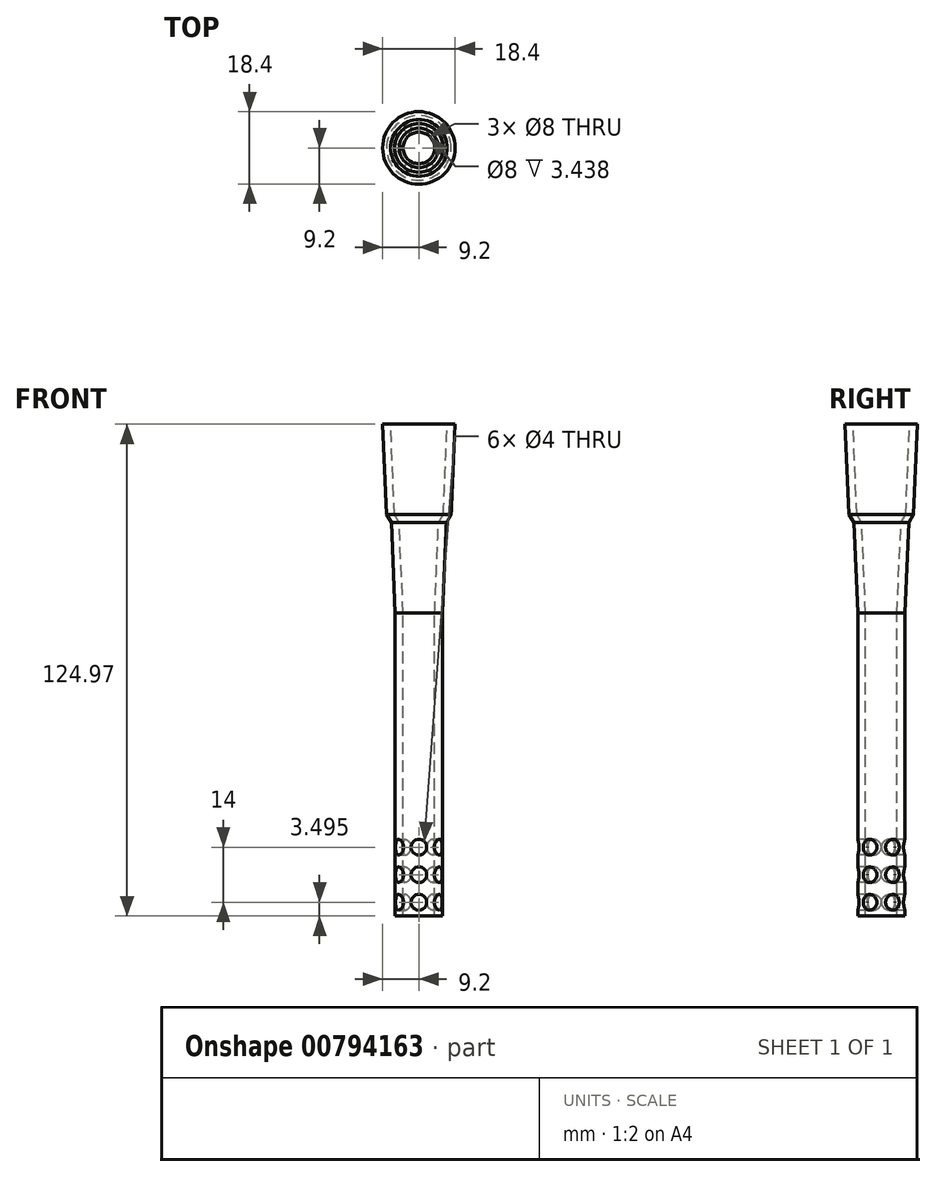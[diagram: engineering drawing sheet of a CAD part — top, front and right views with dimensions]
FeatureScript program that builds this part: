
annotation { "Feature Type Name" : "Feature", "Feature Type Description" : "" }
export const myFeature = defineFeature(function(context is Context, id is Id, definition is map)
    precondition{}
    {
        {
            var Q0;
            Q0=qCreatedBy(makeId("Front.planeOp"),FACE);
            var sketch = newSketch(context, id + "F0", { "sketchPlane" : qUnion([Q0])});
            skLineSegment(sketch, "E0.bottom", {"start": v(0, 29.63) * mm, "end": v(-6, 29.63) * mm});
            skLineSegment(sketch, "E0.top", {"start": v(0, -47.37) * mm, "end": v(-6, -47.37) * mm});
            skLineSegment(sketch, "E0.left", {"start": v(0, 29.63) * mm, "end": v(0, -47.37) * mm});
            skLineSegment(sketch, "E0.right", {"start": v(-6, 29.63) * mm, "end": v(-6, -47.37) * mm});
            skLineSegment(sketch, "E1", {"start": v(-6, 29.63) * mm, "end": v(-7, 52.6) * mm});
            skLineSegment(sketch, "E2", {"start": v(-7, 52.6) * mm, "end": v(0, 52.6) * mm});
            skLineSegment(sketch, "E3", {"start": v(0, 52.6) * mm, "end": v(0, 29.63) * mm});
            skLineSegment(sketch, "E4", {"start": v(0, 77.6) * mm, "end": v(0, 52.6) * mm});
            skLineSegment(sketch, "E5", {"start": v(-5, 52.6) * mm, "end": v(-4, 29.63) * mm});
            skLineSegment(sketch, "E6", {"start": v(-4, 29.63) * mm, "end": v(-4, -47.37) * mm});
            skLineSegment(sketch, "E7", {"start": v(0, 77.6) * mm, "end": v(-7.2, 77.6) * mm});
            skLineSegment(sketch, "E8", {"start": v(-7.2, 77.6) * mm, "end": v(-6.2, 54.63) * mm});
            skLineSegment(sketch, "E9", {"start": v(-6.2, 54.63) * mm, "end": v(0, 54.63) * mm});
            skPoint(sketch, "E9.endSnap0", {"position": v(0, 65.1) * mm});
            skLineSegment(sketch, "E10", {"start": v(-7.2, 77.6) * mm, "end": v(-9.2, 77.6) * mm});
            skLineSegment(sketch, "E11", {"start": v(-9.2, 77.6) * mm, "end": v(-8.2, 54.63) * mm});
            skLineSegment(sketch, "E12", {"start": v(-8.2, 54.63) * mm, "end": v(-6.2, 54.63) * mm});
            skLineSegment(sketch, "E13", {"start": v(-6.2, 54.63) * mm, "end": v(-5, 52.6) * mm});
            skLineSegment(sketch, "E14", {"start": v(-8.2, 54.63) * mm, "end": v(-7, 52.6) * mm});
            skCircle(sketch, "E15", {"center": v(0, -43.87) * mm, "radius": 2 * mm});
            skCircle(sketch, "E16", {"center": v(0, -36.87) * mm, "radius": 2 * mm});
            skCircle(sketch, "E17", {"center": v(0, -29.87) * mm, "radius": 2 * mm});
            skSolve(sketch);
        }
        {
            var Q0;
            Q0=makeQuery(id+"F0.imprint","IMPRINT",FACE,{"disambiguationData":[TD([[makeQuery(id+"F0.imprint","IMPRINT",EDGE,{"derivedFrom":sQuery(id+"F0.wireOp",EDGE,"E8")}),-1.0]])]});
            var Q1;
            Q1=makeQuery(id+"F0.imprint","IMPRINT",FACE,{"disambiguationData":[TD([[makeQuery(id+"F0.imprint","IMPRINT",EDGE,{"derivedFrom":sQuery(id+"F0.wireOp",EDGE,"E12")}),-1.0]])]});
            var Q2;
            {var subQ0=sQuery(id+"F0.wireOp",EDGE,"E1");Q2=makeQuery(id+"F0.imprint","IMPRINT",FACE,{"disambiguationData":[TD([[makeQuery(id+"F0.imprint","IMPRINT",EDGE,{"derivedFrom":subQ0}),-1.0]])]});}
            var Q3;
            {var subQ0=sQuery(id+"F0.wireOp",EDGE,"E0.right");Q3=makeQuery(id+"F0.imprint","IMPRINT",FACE,{"disambiguationData":[TD([[makeQuery(id+"F0.imprint","IMPRINT",EDGE,{"derivedFrom":subQ0}),1.0]])]});}
            var Q4;
            Q4=sQuery(id+"F0.wireOp",EDGE,"E4");
            revolve(context, id + "F1", {"surfaceOperationType" : NewSurfaceOperationType.NEW, "entities" : qUnion([Q0, Q1, Q2, Q3]), "axis" : qUnion([Q4]), "revolveType" : RevolveType.FULL});
        }
        {
            var Q0;
            {var subQ0=sQuery(id+"F0.wireOp",EDGE,"E15");var subQ1=sQuery(id+"F0.wireOp",EDGE,"E0.left");var subQ2=makeQuery(id+"F0.imprint","INTERSECT",VERTEX,{"disambiguationData":[OD(0.0)],"derivedFrom":[subQ1,subQ0]});Q0=makeQuery(id+"F0.imprint","IMPRINT",FACE,{"disambiguationData":[TD([[makeQuery(id+"F0.imprint","IMPRINT",EDGE,{"disambiguationData":[TD([[subQ2,-1.0]])],"derivedFrom":subQ1}),1.0]])]});}
            var Q1;
            {var subQ0=sQuery(id+"F0.wireOp",EDGE,"E15");var subQ1=sQuery(id+"F0.wireOp",EDGE,"E0.left");var subQ2=makeQuery(id+"F0.imprint","INTERSECT",VERTEX,{"disambiguationData":[OD(0.0)],"derivedFrom":[subQ1,subQ0]});Q1=makeQuery(id+"F0.imprint","IMPRINT",FACE,{"disambiguationData":[TD([[makeQuery(id+"F0.imprint","IMPRINT",EDGE,{"disambiguationData":[TD([[subQ2,-1.0]])],"derivedFrom":subQ1}),-1.0]])]});}
            var Q2;
            {var subQ0=sQuery(id+"F0.wireOp",EDGE,"E16");var subQ1=sQuery(id+"F0.wireOp",EDGE,"E0.left");var subQ2=makeQuery(id+"F0.imprint","INTERSECT",VERTEX,{"disambiguationData":[OD(0.0)],"derivedFrom":[subQ1,subQ0]});Q2=makeQuery(id+"F0.imprint","IMPRINT",FACE,{"disambiguationData":[TD([[makeQuery(id+"F0.imprint","IMPRINT",EDGE,{"disambiguationData":[TD([[subQ2,-1.0]])],"derivedFrom":subQ1}),-1.0]])]});}
            var Q3;
            {var subQ0=sQuery(id+"F0.wireOp",EDGE,"E16");var subQ1=sQuery(id+"F0.wireOp",EDGE,"E0.left");var subQ2=makeQuery(id+"F0.imprint","INTERSECT",VERTEX,{"disambiguationData":[OD(0.0)],"derivedFrom":[subQ1,subQ0]});Q3=makeQuery(id+"F0.imprint","IMPRINT",FACE,{"disambiguationData":[TD([[makeQuery(id+"F0.imprint","IMPRINT",EDGE,{"disambiguationData":[TD([[subQ2,-1.0]])],"derivedFrom":subQ1}),1.0]])]});}
            var Q4;
            {var subQ0=sQuery(id+"F0.wireOp",EDGE,"E17");var subQ1=sQuery(id+"F0.wireOp",EDGE,"E0.left");var subQ2=makeQuery(id+"F0.imprint","INTERSECT",VERTEX,{"disambiguationData":[OD(0.0)],"derivedFrom":[subQ1,subQ0]});Q4=makeQuery(id+"F0.imprint","IMPRINT",FACE,{"disambiguationData":[TD([[makeQuery(id+"F0.imprint","IMPRINT",EDGE,{"disambiguationData":[TD([[subQ2,-1.0]])],"derivedFrom":subQ1}),1.0]])]});}
            var Q5;
            {var subQ0=sQuery(id+"F0.wireOp",EDGE,"E17");var subQ1=sQuery(id+"F0.wireOp",EDGE,"E0.left");var subQ2=makeQuery(id+"F0.imprint","INTERSECT",VERTEX,{"disambiguationData":[OD(0.0)],"derivedFrom":[subQ1,subQ0]});Q5=makeQuery(id+"F0.imprint","IMPRINT",FACE,{"disambiguationData":[TD([[makeQuery(id+"F0.imprint","IMPRINT",EDGE,{"disambiguationData":[TD([[subQ2,-1.0]])],"derivedFrom":subQ1}),-1.0]])]});}
            extrude(context, id + "F2", {"entities" : qUnion([Q0, Q1, Q2, Q3, Q4, Q5]), "oppositeDirection" : true, "depth" : 25 * mm, "offsetDistance" : 25 * mm, "symmetric" : true});
        }
        {
            var Q0;
            Q0=makeQuery(id+"F2.opExtrude","SWEPT_BODY",BODY,{"disambiguationData":[OSD([sQuery(id+"F0.wireOp",EDGE,"E15")])]});
            var Q1;
            Q1=makeQuery(id+"F2.opExtrude","SWEPT_BODY",BODY,{"disambiguationData":[OSD([sQuery(id+"F0.wireOp",EDGE,"E16")])]});
            var Q2;
            Q2=makeQuery(id+"F2.opExtrude","SWEPT_BODY",BODY,{"disambiguationData":[OSD([sQuery(id+"F0.wireOp",EDGE,"E17")])]});
            var Q3;
            Q3=sQuery(id+"F0.wireOp",EDGE,"E0.left");
            circularPattern(context, id + "F3", {"operationType" : NewBodyOperationType.REMOVE, "entities" : qUnion([Q0, Q1, Q2]), "axis" : qUnion([Q3]), "angle" : 360 * degree, "instanceCount" : 3, "equalSpace" : true, "computeTransformsWithoutBuiltin" : true});
        }
    });
